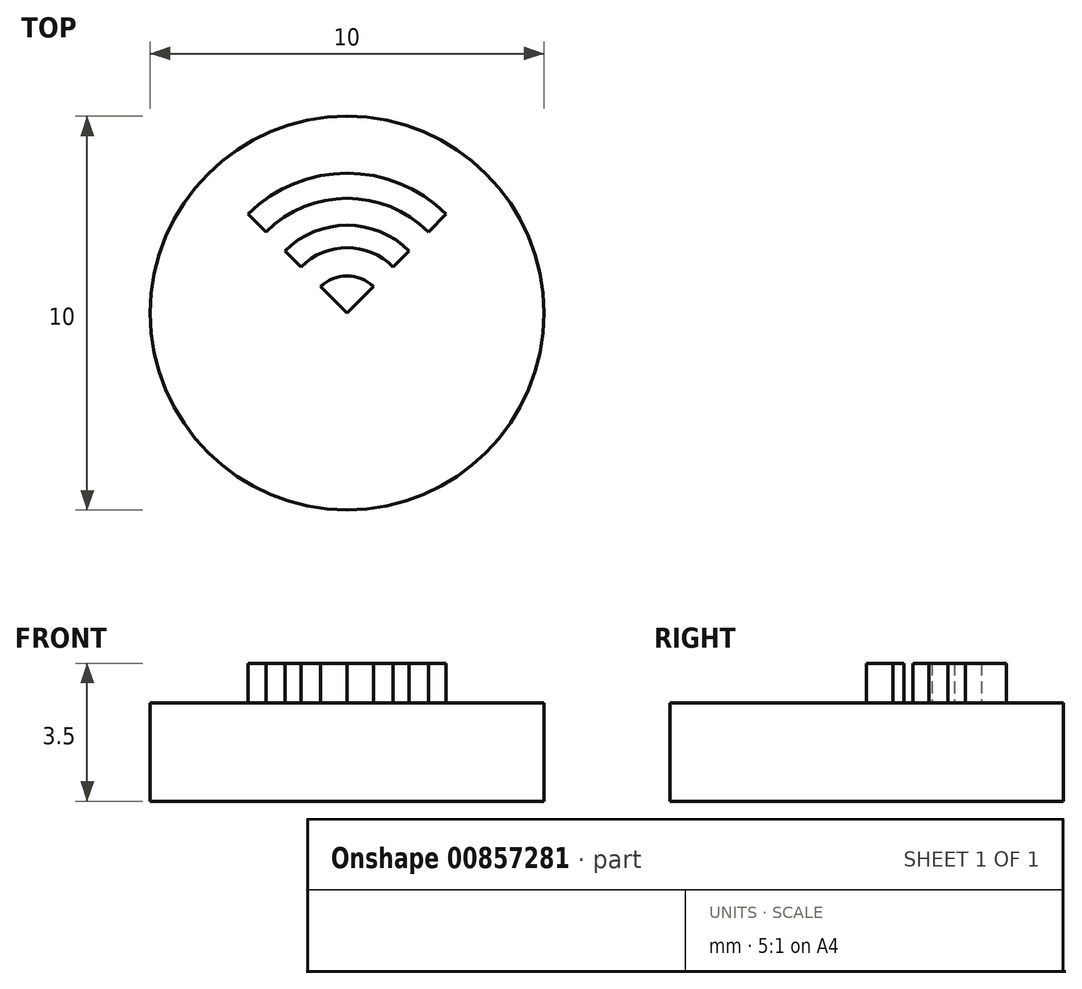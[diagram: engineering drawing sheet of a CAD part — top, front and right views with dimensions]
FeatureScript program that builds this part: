
annotation { "Feature Type Name" : "Feature", "Feature Type Description" : "" }
export const myFeature = defineFeature(function(context is Context, id is Id, definition is map)
    precondition{}
    {
        {
            var Q0;
            Q0=qCreatedBy(makeId("Top.planeOp"),FACE);
            var sketch = newSketch(context, id + "F0", { "sketchPlane" : qUnion([Q0])});
            skCircle(sketch, "E0", {"center": v(0, 0) * mm, "radius": 5 * mm});
            skSolve(sketch);
        }
        {
            var Q0;
            Q0=qSketchRegion(id+"F0",true);
            extrude(context, id + "F1", {"entities" : qUnion([Q0]), "depth" : 2.5 * mm, "offsetDistance" : 25 * mm});
        }
        {
            var Q0;
            Q0=makeQuery(id+"F1.opExtrude","CAP_FACE",FACE,{"disambiguationData":[OSD([sQuery(id+"F0.wireOp",EDGE,"E0")])],"isStart":false});
            var sketch = newSketch(context, id + "F2", { "sketchPlane" : qUnion([Q0])});
            skArc(sketch, "E1", {"start": v(2.51, 2.51) * mm, "mid": v(0, 3.55) * mm, "end": v(-2.51, 2.51) * mm});
            skArc(sketch, "E2", {"start": v(2.06, 2.06) * mm, "mid": v(0, 2.92) * mm, "end": v(-2.06, 2.06) * mm});
            skArc(sketch, "E3", {"start": v(1.58, 1.58) * mm, "mid": v(0, 2.23) * mm, "end": v(-1.58, 1.58) * mm});
            skArc(sketch, "E4", {"start": v(1.17, 1.17) * mm, "mid": v(0, 1.66) * mm, "end": v(-1.17, 1.17) * mm});
            skArc(sketch, "E5", {"start": v(0.67, 0.67) * mm, "mid": v(0, 0.95) * mm, "end": v(-0.67, 0.67) * mm});
            skLineSegment(sketch, "E6", {"start": v(0, 0) * mm, "end": v(0.67, 0.67) * mm});
            skLineSegment(sketch, "E7.MirrorCS", {"start": v(0, 0) * mm, "end": v(-0.67, 0.67) * mm});
            skLineSegment(sketch, "E8.trimOffspring", {"start": v(-2.06, 2.06) * mm, "end": v(-2.51, 2.51) * mm});
            skLineSegment(sketch, "E9.trimOffspring", {"start": v(-1.17, 1.17) * mm, "end": v(-1.58, 1.58) * mm});
            skLineSegment(sketch, "E10.trimOffspring", {"start": v(1.17, 1.17) * mm, "end": v(1.58, 1.58) * mm});
            skLineSegment(sketch, "E11.trimOffspring", {"start": v(2.06, 2.06) * mm, "end": v(2.51, 2.51) * mm});
            skSolve(sketch);
        }
        {
            var Q0;
            Q0 = qSketchRegion(id + "F2", true);
            extrude(context, id + "F3", {"entities" : qUnion([Q0]), "operationType" : NewBodyOperationType.ADD, "depth" : 1 * mm, "offsetDistance" : 25 * mm});
        }
    });
